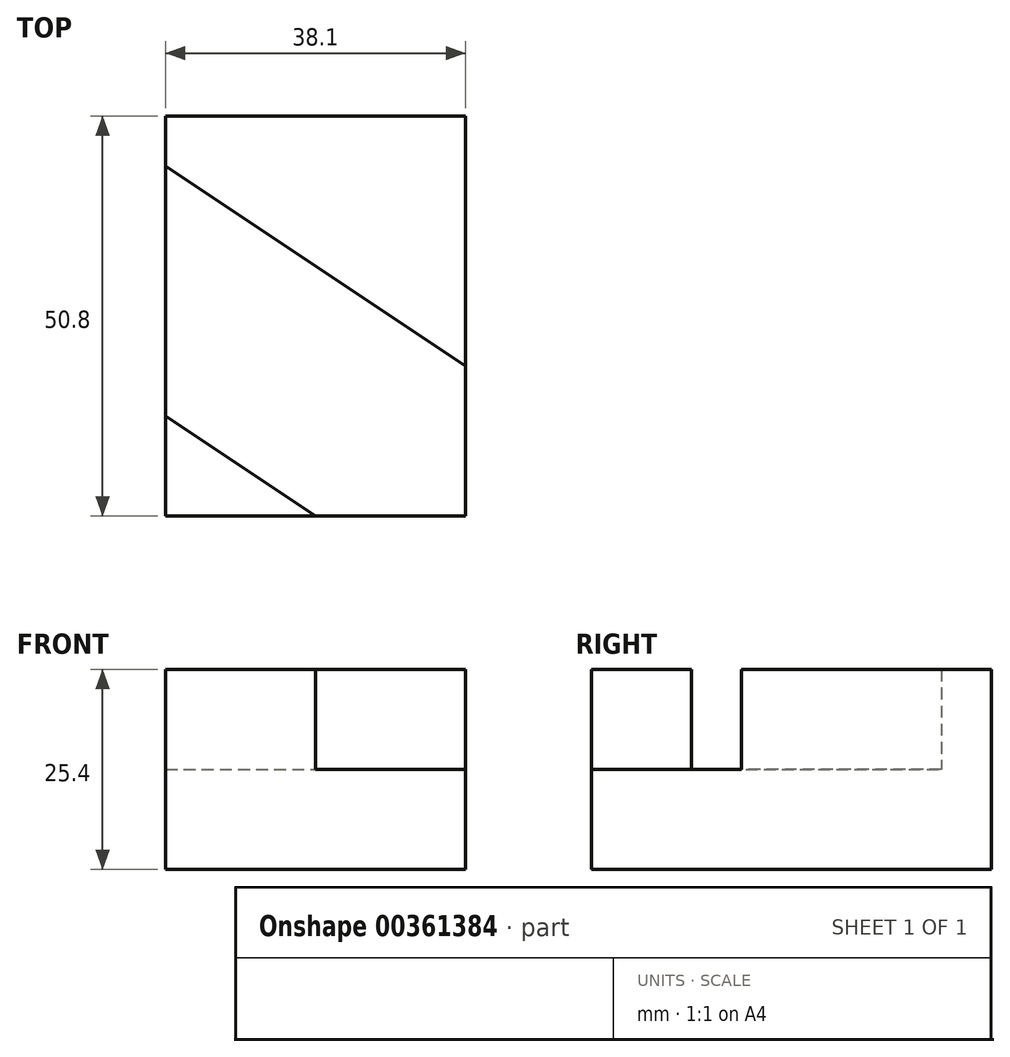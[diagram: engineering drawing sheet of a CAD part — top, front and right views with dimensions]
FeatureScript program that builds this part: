
annotation { "Feature Type Name" : "Feature", "Feature Type Description" : "" }
export const myFeature = defineFeature(function(context is Context, id is Id, definition is map)
    precondition{}
    {
        {
            var Q0;
            Q0=qCreatedBy(makeId("Top.planeOp"),FACE);
            var sketch = newSketch(context, id + "F0", { "sketchPlane" : qUnion([Q0])});
            skLineSegment(sketch, "E0", {"start": v(-54.1, 0) * mm, "end": v(-54.1, 50.8) * mm});
            skLineSegment(sketch, "E1", {"start": v(-54.1, 50.8) * mm, "end": v(-16, 50.8) * mm});
            skLineSegment(sketch, "E2", {"start": v(-16, 50.8) * mm, "end": v(-16, 0) * mm});
            skLineSegment(sketch, "E3", {"start": v(-16, 0) * mm, "end": v(-54.1, 0) * mm});
            skSolve(sketch);
        }
        {
            var Q0;
            Q0 = qSketchRegion(id + "F0", true);
            extrude(context, id + "F1", {"entities" : qUnion([Q0]), "oppositeDirection" : true, "depth" : 12.7 * mm});
        }
        {
            var Q0;
            Q0=makeQuery(id+"F1.opExtrude","CAP_FACE",FACE,{"disambiguationData":[OSD([sQuery(id+"F0.wireOp",EDGE,"E0"),sQuery(id+"F0.wireOp",EDGE,"E1"),sQuery(id+"F0.wireOp",EDGE,"E2"),sQuery(id+"F0.wireOp",EDGE,"E3")])],"isStart":true});
            var sketch = newSketch(context, id + "F2", { "sketchPlane" : qUnion([Q0])});
            skLineSegment(sketch, "E4", {"start": v(-54.1, 50.8) * mm, "end": v(-54.1, 44.45) * mm});
            skLineSegment(sketch, "E5", {"start": v(-54.1, 44.45) * mm, "end": v(-16, 19.05) * mm});
            skLineSegment(sketch, "E6", {"start": v(-16, 19.05) * mm, "end": v(-16, 50.8) * mm});
            skLineSegment(sketch, "E7", {"start": v(-16, 50.8) * mm, "end": v(-54.1, 50.8) * mm});
            skSolve(sketch);
        }
        {
            var Q0;
            Q0 = qSketchRegion(id + "F2", true);
            extrude(context, id + "F3", {"entities" : qUnion([Q0]), "operationType" : NewBodyOperationType.ADD, "depth" : 12.7 * mm});
        }
        {
            var Q0;
            Q0=makeQuery(id+"F1.opExtrude","CAP_FACE",FACE,{"disambiguationData":[OSD([sQuery(id+"F0.wireOp",EDGE,"E0"),sQuery(id+"F0.wireOp",EDGE,"E1"),sQuery(id+"F0.wireOp",EDGE,"E2"),sQuery(id+"F0.wireOp",EDGE,"E3")])],"isStart":true});
            var sketch = newSketch(context, id + "F4", { "sketchPlane" : qUnion([Q0])});
            skLineSegment(sketch, "E8", {"start": v(-54.1, 12.7) * mm, "end": v(-35.04, 0) * mm});
            skLineSegment(sketch, "E9", {"start": v(-35.04, 0) * mm, "end": v(-54.1, 0) * mm});
            skLineSegment(sketch, "E10", {"start": v(-54.1, 0) * mm, "end": v(-54.1, 12.7) * mm});
            skSolve(sketch);
        }
        {
            var Q0;
            Q0 = qSketchRegion(id + "F4", true);
            extrude(context, id + "F5", {"entities" : qUnion([Q0]), "operationType" : NewBodyOperationType.ADD, "depth" : 12.7 * mm});
        }
    });
